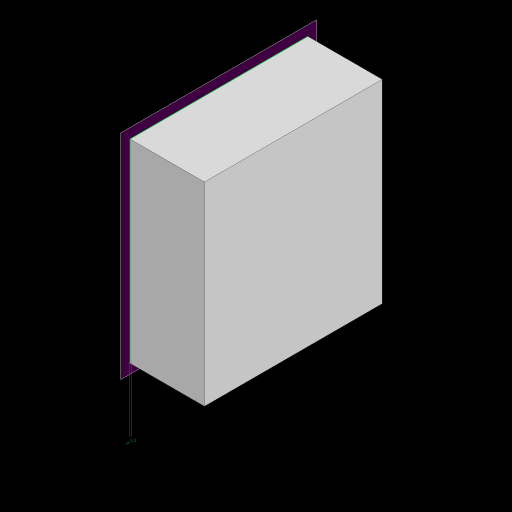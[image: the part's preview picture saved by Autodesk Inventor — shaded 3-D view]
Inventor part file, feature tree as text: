
AUTODESK INVENTOR PART (.ipt)
format: ipt  version: 2023 (Build 270158000, 158)  size: 290,304 bytes
history: native  units: in
note: dims shown in document units (in); Inventor stores cm internally (conversion verified against a paired STEP export)
features: sketch x10, extrude x9, projected_geometry x5, plane x2, fillet x2, split x1
ambient origin geometry x8: Origin, YZ Plane, XZ Plane, XY Plane, X Axis, Y Axis, Z Axis, Center Point
bodies: Solid1 (feature_tree)
feature tree (29):
  extrude  "Extrusion1"  Depth=3.937in
  sketch  "Sketch2"  dims[d2=5.1181in d3=0.0in d4=0.315in d5=0.0in]
  extrude  "Extrusion2"  Depth=0.315in TaperAngle=0.0deg
  extrude  "Extrusion3"  Depth=3.937in
  plane  "Work Plane1"
  extrude  "Extrusion4"  Depth=5.1181in
  fillet  "Fillet1"  Radius=5.1181in
  sketch  "Sketch8"  dims[d8=1.9685in d9=2.5591in d10=5.1181in]
  extrude  "Extrusion10"  Depth=0.1496in
  extrude  "Extrusion11"  [1 undecoded]
  fillet  "Fillet2"  Radius=0.1969in
  extrude  "Extrusion12"  Depth=0.1969in
  extrude  "Extrusion13"  Depth=3.5433in TaperAngle=0.0deg
  extrude  "Extrusion14"  Depth=0.1969in TaperAngle=0.0deg
  plane  "Work Plane2"
  split  "Split1"
  sketch  "Sketch18"  dims[d82=4.685in d84=5.0in d85=0.0in d86=0.1969in d87=45.0deg d88=45.0deg d90=45.0deg d91=45.0deg d92=0.7874in d93=0.9843in d94=0.7874in d95=0.9843in d96=0.0394in d97=3.3465in d98=4.3307in d99=3.5433in d100=0.0984in d101=0.1575in d102=0.1693in d103=0.1417in d104=0.1969in d105=0.1693in d107=4.7244in d108=0.1969in d109=0.1575in d110=0.1417in d111=0.1969in d112=0.1417in d113=0.1969in d114=0.1417in d115=0.1969in d116=0.1181in d117=0.0in d118=0.7087in d119=0.1181in d121=0.7087in d122=1.3386in d123=0.7874in d124=0.0in d125=45.0deg d126=2.874in d129=3.5433in d130=0.1673in d131=0.1417in d135=0.1417in d136=0.1417in d137=0.1417in d138=1.5748in d139=0.0in d140=0.0512in]
  sketch  "Sketch1"  dims[d0=4.685in d1=3.937in]
  sketch  "Sketch3"  dims[d6=3.5433in d7=3.937in]
  projected_geometry  "Projected Loop1"
  sketch  "Sketch10"  dims[d11=2.874in d12=0.1496in]
  projected_geometry  "Projected Loop2"
  sketch  "Sketch12"  dims[d13=0.7087in d14=0.0in d15=-0.1969in d16=0.1969in]
  projected_geometry  "Projected Loop4"
  sketch  "Sketch13"  dims[d17=0.1969in d18=0.1969in]
  sketch  "Sketch14"  dims[d19=3.5433in d20=0.0in d21=3.5433in d22=0.0in]
  sketch  "Sketch15"  dims[d23=0.1969in d74=0.1969in d75=0.0in]
  projected_geometry  "Projected Loop5"
  projected_geometry  "Project Cut Edges1"
note: 1 required parameter value undecoded (feature->parameter linkage not recoverable at this tier; creation-order binding heuristic only, values carry confidence <= 0.55)
